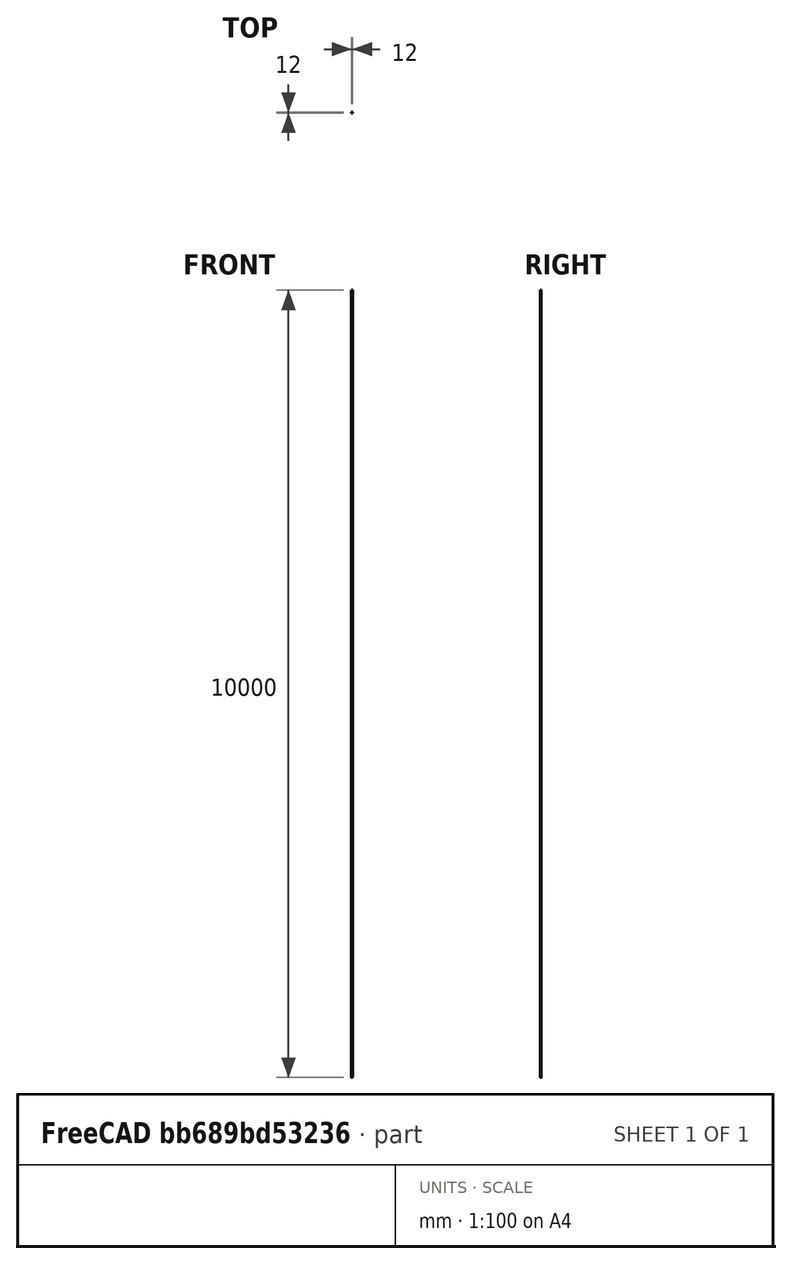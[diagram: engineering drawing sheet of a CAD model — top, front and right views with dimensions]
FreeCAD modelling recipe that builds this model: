
FCSTD DOCUMENT  (FreeCAD 0.16R)
Label: PrestaToShraderWasher
License: All rights reserved
LicenseURL: http://en.wikipedia.org/wiki/All_rights_reserved
objects: Sketcher::SketchObject×3, PartDesign::Pad×2, PartDesign::Pocket×1, Mesh::Feature×1
note: 9 computed .brp shape members not serialized (recipe doc carries the construction recipe); baked Part::Feature solids carry a one-line shape summary decoded from their .brp

FEATURE [Sketcher::SketchObject] Sketch
  sketch-geometry (1):
    g0: Circle CenterX=0 CenterY=0 CenterZ=0 NormalX=0 NormalY=0 NormalZ=1 Radius=6
  constraints (2):
    c: Radius(g0) = 6
    c: Coincident(g0,g-1)
FEATURE [PartDesign::Pad] Pad
  Length = 1.5
  Length2 = 100
  Sketch = -> Sketch
  Type = 0
FEATURE [Sketcher::SketchObject] Sketch001
  Placement = pos=(0,0,0) rot=(1,0,0;3.14159rad)
  Support = -> Pad [Face2]
  sketch-geometry (1):
    g0: Circle CenterX=0 CenterY=0 CenterZ=0 NormalX=0 NormalY=0 NormalZ=1 Radius=4
  constraints (2):
    c: Coincident(g0,g-1)
    c: Radius(g0) = 4
FEATURE [PartDesign::Pad] Pad001
  Length = 1.5
  Length2 = 100
  Sketch = -> Sketch001
  Type = 0
FEATURE [Sketcher::SketchObject] Sketch002
  Placement = pos=(0,0,-1.5) rot=(1,0,0;3.14159rad)
  Support = -> Pad001 [Face5]
  sketch-geometry (1):
    g0: Circle CenterX=0 CenterY=0 CenterZ=0 NormalX=0 NormalY=0 NormalZ=1 Radius=3.5
  constraints (2):
    c: Coincident(g0,g-1)
    c: Radius(g0) = 3.5
FEATURE [PartDesign::Pocket] Pocket
  Length = 5
  Sketch = -> Sketch002
  Type = 1
FEATURE [Mesh::Feature] Mesh  label="Pocket (Meshed)"
